# Revit family: C981Q (FINAL)
name_source: partatom
category: Generic Models
revit_build: Autodesk Revit Architecture 2012 (Build: 20110309_2315(x64)
units: mm (PartAtom-declared; Revit-internal decimal feet)

## types (1)
- C981Q (FINAL)
    CONNECTIVITY- Input Terminals- Analog = none
    CONNECTIVITY- Input Terminals- Audio = 3.5mm Audio Mini Jack x2, DisplayPort Audio x2, HDMI Audio x3
    CONNECTIVITY- Input Terminals- Data = microSD (Media Player), USB 2.0 (Media Player), USB 2.0 (Service), USB Type-B (Upstream), USB 2.0 x2 (Compute Module, USB CM1 is Powered 5V/2A)
    CONNECTIVITY- Input Terminals- Digital = HDMI 2.0 x2 (with HDCP), DVI-D (with HDCP), DisplayPort x2 (with HDCP)
    CONNECTIVITY- Input Terminals- External Control = LAN (100Mbit), 3.5 Mini Jack IR Remote, RS232C
    CONNECTIVITY- Output Terminals- Audio = 3.5mm Mini Jack, HDMI Audio x3, DisplayPort Audio x2
    CONNECTIVITY- Output Terminals- Digital = HDMI 2.0x3 (with HDCP), DisplayPort 1.2x2 (with HDCP)
    CONNECTIVITY- Output Terminals- External Control = LAN (100mb)
    Description = NEC Ultra High Definition Large Format Display
    ENVIRONMENTAL CONDITIONS- Operating Altitude = 3000m (9843ft)
    ENVIRONMENTAL CONDITIONS- Operating Humidity = 20 - 80%
    ENVIRONMENTAL CONDITIONS- Operating Temperature = 0 to 40 C
    LCD MODULE- Aspect Ratio = 16 : 9
    LCD MODULE- Brightness (Typical/Minimum) = 245 cd/sqm / 350 cd/sqm
    LCD MODULE- Contrast Ratio (Typical) = 1300:1 native, not included localized dimming
    LCD MODULE- Displayable Colors = Over 1.07 Billion
    LCD MODULE- Native Resolution = 3840 x 2160
    LCD MODULE- Orientation = Landscape and Portrait
    LCD MODULE- Panel Haze (%) = 28
    LCD MODULE- Panel Technology = D-LED, S-IPS
    LCD MODULE- Viewable Image Size = 98"
    LCD MODULE- Viewing Angle = 178deg Vert., 178deg Hor (89U/89D/89L/89R) @ CR>10
    Manufacturer = NEC Display Solutions
    Model = C981Q
    PHYSICAL SPECS- Bezel Width (L/R, T/B) = 1590.0mm / 1590.0mm / 1590.0mm / 1590.0mm
    PHYSICAL SPECS- Net Dimensions (w/o Stand, WxHxD) = 86.4 x 49.2 x 3.7in. / 2193.8 x 1248.8 x 93.0mm
    PHYSICAL SPECS- Net Weight (w/o Stand) = 198.6 lbs. / 90.0 kg
    PHYSICAL SPECS- Vesa Hole Configuration = 8x M8 x 16mm (600 x 400, 400 x 400)
    POWER CONSUMPTION- Current Rating = 6.1A @ 100V, 2.6A @ 240V
    POWER CONSUMPTION- Network Standby = 2W
    POWER CONSUMPTION- Normal Standby = 0.5W
    POWER CONSUMPTION- On (Typ/Max Bightness/Overall Max) = 240W/380W/525W
    POWER CONSUMPTION- Speaker Rating = Integrated 10W x 10W, Optional 15W x 2
    SENSORS- Ambient Light Sensor = Integrated and programmable
    SENSORS- Human Sensor = Optional through KT-RC2 Accessory
    SENSORS- NFC Sensor = Integrated; works in conjunction with free NEC Intelligent Wireless Data Application
    SENSORS- Temperature Sensor = Integrated and programmable; linked to cooling fans
    URL = www.necdisplay.com

## geometry (parser evidence)
native form markers: Sweep x1
no freeform markers — native parametric forms only
